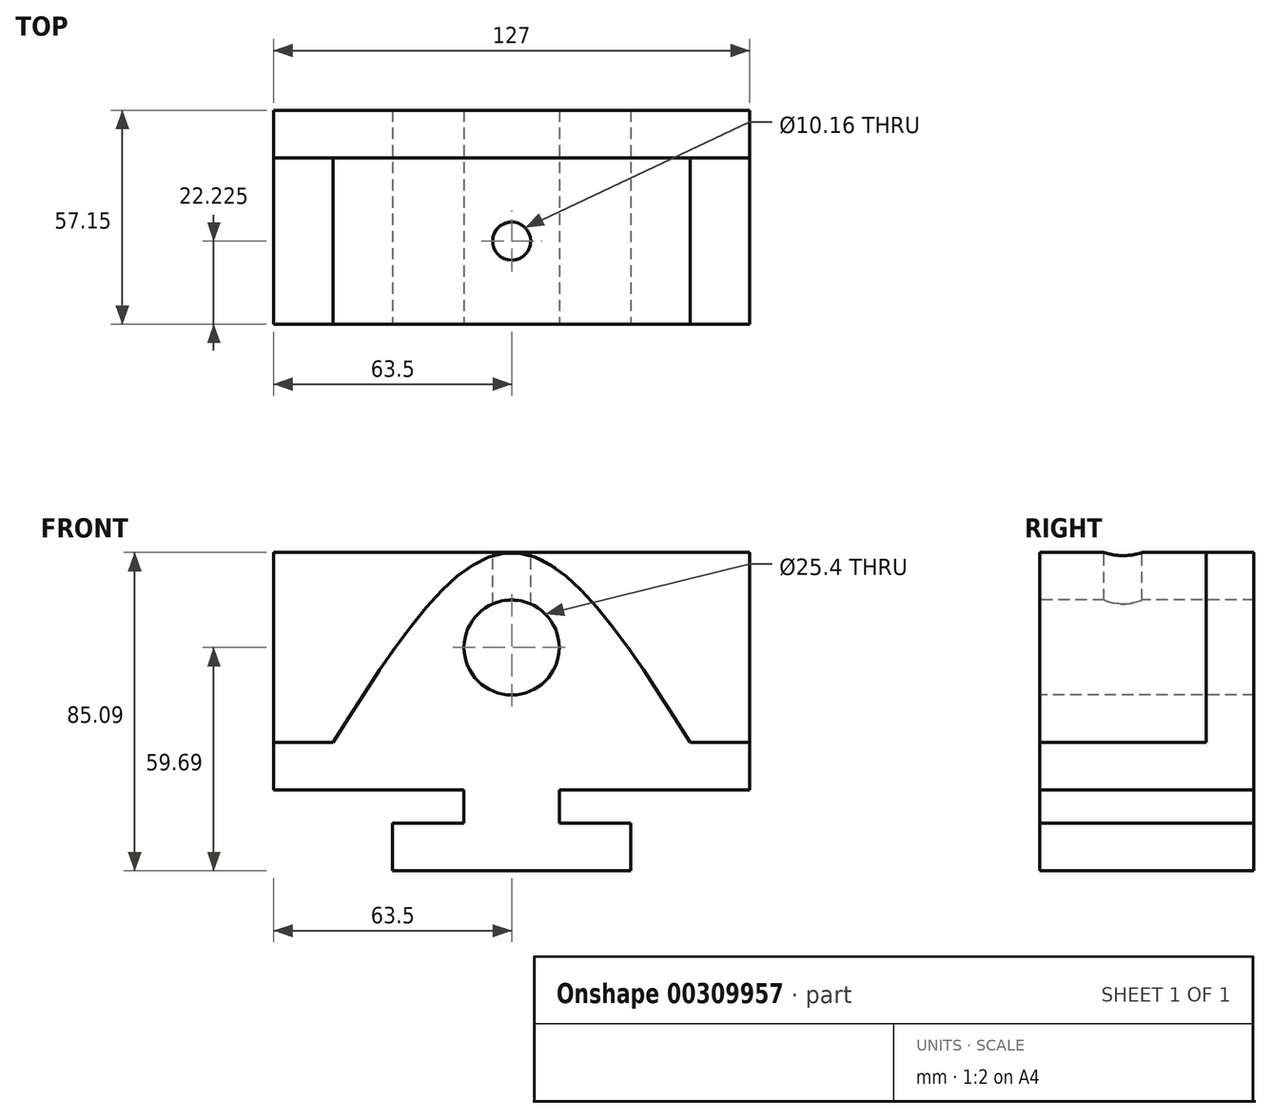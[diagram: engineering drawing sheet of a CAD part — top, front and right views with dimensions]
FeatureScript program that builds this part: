
annotation { "Feature Type Name" : "Feature", "Feature Type Description" : "" }
export const myFeature = defineFeature(function(context is Context, id is Id, definition is map)
    precondition{}
    {
        {
            var Q0;
            Q0=qCreatedBy(makeId("Front.planeOp"),FACE);
            var sketch = newSketch(context, id + "F0", { "sketchPlane" : qUnion([Q0])});
            skLineSegment(sketch, "E0", {"start": v(0, 0) * mm, "end": v(127, 0) * mm});
            skLineSegment(sketch, "E1", {"start": v(127, 0) * mm, "end": v(127, 85.1) * mm});
            skLineSegment(sketch, "E2", {"start": v(127, 85.1) * mm, "end": v(0, 85.1) * mm});
            skLineSegment(sketch, "E3", {"start": v(0, 85.1) * mm, "end": v(0, 0) * mm});
            skSolve(sketch);
        }
        {
            var Q0;
            Q0=makeQuery(id+"F0.imprint","IMPRINT",FACE,{"disambiguationData":[TD([[makeQuery(id+"F0.imprint","IMPRINT",EDGE,{"derivedFrom":sQuery(id+"F0.wireOp",EDGE,"E0")}),1.0]])]});
            extrude(context, id + "F1", {"entities" : qUnion([Q0]), "oppositeDirection" : true, "depth" : 57.15 * mm});
        }
        {
            var Q0;
            Q0=makeQuery(id+"F1.opExtrude","CAP_FACE",FACE,{"disambiguationData":[OSD([sQuery(id+"F0.wireOp",EDGE,"E0"),sQuery(id+"F0.wireOp",EDGE,"E1"),sQuery(id+"F0.wireOp",EDGE,"E2"),sQuery(id+"F0.wireOp",EDGE,"E3")])],"isStart":true});
            var sketch = newSketch(context, id + "F2", { "sketchPlane" : qUnion([Q0])});
            skLineSegment(sketch, "E4", {"start": v(0, 0) * mm, "end": v(63.5, 0) * mm, "construction": true});
            skLineSegment(sketch, "E5", {"start": v(63.5, 0) * mm, "end": v(95.25, 0) * mm});
            skLineSegment(sketch, "E6", {"start": v(95.25, 0) * mm, "end": v(95.25, 12.7) * mm});
            skLineSegment(sketch, "E7", {"start": v(95.25, 12.7) * mm, "end": v(76.2, 12.7) * mm});
            skLineSegment(sketch, "E8", {"start": v(76.2, 12.7) * mm, "end": v(76.2, 21.59) * mm});
            skLineSegment(sketch, "E9", {"start": v(76.2, 21.59) * mm, "end": v(127, 21.59) * mm});
            skLineSegment(sketch, "E10", {"start": v(127, 21.59) * mm, "end": v(127, 34.3) * mm});
            skLineSegment(sketch, "E11", {"start": v(127, 34.3) * mm, "end": v(111.12, 34.3) * mm});
            skLineSegment(sketch, "E12", {"start": v(63.5, 0) * mm, "end": v(31.75, 0) * mm});
            skLineSegment(sketch, "E13", {"start": v(31.75, 0) * mm, "end": v(31.75, 12.7) * mm});
            skLineSegment(sketch, "E14", {"start": v(31.75, 12.7) * mm, "end": v(50.8, 12.7) * mm});
            skLineSegment(sketch, "E15", {"start": v(50.8, 12.7) * mm, "end": v(50.8, 21.59) * mm});
            skLineSegment(sketch, "E16", {"start": v(50.8, 21.59) * mm, "end": v(0, 21.59) * mm});
            skLineSegment(sketch, "E17", {"start": v(0, 21.59) * mm, "end": v(0, 34.29) * mm});
            skLineSegment(sketch, "E18", {"start": v(0, 34.29) * mm, "end": v(15.88, 34.29) * mm});
            skFitSpline(sketch, "E19", {"points": [v(15.88, 34.29) * mm, v(63.5, 85.1) * mm, v(111.12, 34.3) * mm], "startDerivative": vector(95.25, 152.4) * mm, "endDerivative": vector(95.25, -152.4) * mm});
            skCircle(sketch, "E20", {"center": v(63.5, 59.7) * mm, "radius": 12.7 * mm});
            skSolve(sketch);
        }
        {
            var Q0;
            {var subQ1=sQuery(id+"F2.wireOp",EDGE,"E6");Q0=makeQuery(id+"F2.imprint","IMPRINT",FACE,{"disambiguationData":[TD([[makeQuery(id+"F2.imprint","IMPRINT",EDGE,{"derivedFrom":subQ1}),-1.0]])]});}
            var Q1;
            {var subQ1=sQuery(id+"F2.wireOp",EDGE,"E13");Q1=makeQuery(id+"F2.imprint","IMPRINT",FACE,{"disambiguationData":[TD([[makeQuery(id+"F2.imprint","IMPRINT",EDGE,{"derivedFrom":subQ1}),1.0]])]});}
            var Q2;
            Q2=makeQuery(id+"F2.imprint","IMPRINT",FACE,{"disambiguationData":[TD([[makeQuery(id+"F2.imprint","IMPRINT",EDGE,{"derivedFrom":sQuery(id+"F2.wireOp",EDGE,"E20")}),1.0]])]});
            extrude(context, id + "F3", {"entities" : qUnion([Q0, Q1, Q2]), "operationType" : NewBodyOperationType.REMOVE, "oppositeDirection" : true, "depth" : 57.15 * mm});
        }
        {
            var Q0;
            Q0=makeQuery(id+"F1.opExtrude","SWEPT_FACE",FACE,{"disambiguationData":[OSD([sQuery(id+"F0.wireOp",EDGE,"E2")])]});
            var sketch = newSketch(context, id + "F4", { "sketchPlane" : qUnion([Q0])});
            skLineSegment(sketch, "E21", {"start": v(0, 0) * mm, "end": v(63.5, 0) * mm, "construction": true});
            skLineSegment(sketch, "E22", {"start": v(63.5, 0) * mm, "end": v(63.5, 22.23) * mm, "construction": true});
            skCircle(sketch, "E23", {"center": v(63.5, 22.23) * mm, "radius": 5.08 * mm});
            skSolve(sketch);
        }
        {
            var Q0;
            Q0=makeQuery(id+"F4.imprint","IMPRINT",FACE,{"disambiguationData":[TD([[makeQuery(id+"F4.imprint","IMPRINT",EDGE,{"derivedFrom":sQuery(id+"F4.wireOp",EDGE,"E23")}),1.0]])]});
            var Q1;
            Q1=sQuery(id+"F4.wireOp",EDGE,"E23");
            extrude(context, id + "F5", {"entities" : qUnion([Q0]), "operationType" : NewBodyOperationType.REMOVE, "surfaceEntities" : qUnion([Q1]), "oppositeDirection" : true, "depth" : 25.4 * mm});
        }
        {
            var Q0;
            {var subQ0=sQuery(id+"F2.wireOp",EDGE,"E18");Q0=makeQuery(id+"F2.imprint","IMPRINT",FACE,{"disambiguationData":[TD([[makeQuery(id+"F2.imprint","IMPRINT",EDGE,{"derivedFrom":subQ0}),1.0]])]});}
            var Q1;
            {var subQ0=sQuery(id+"F2.wireOp",EDGE,"E11");Q1=makeQuery(id+"F2.imprint","IMPRINT",FACE,{"disambiguationData":[TD([[makeQuery(id+"F2.imprint","IMPRINT",EDGE,{"derivedFrom":subQ0}),-1.0]])]});}
            extrude(context, id + "F6", {"entities" : qUnion([Q0, Q1]), "operationType" : NewBodyOperationType.REMOVE, "oppositeDirection" : true, "depth" : 44.45 * mm});
        }
    });
